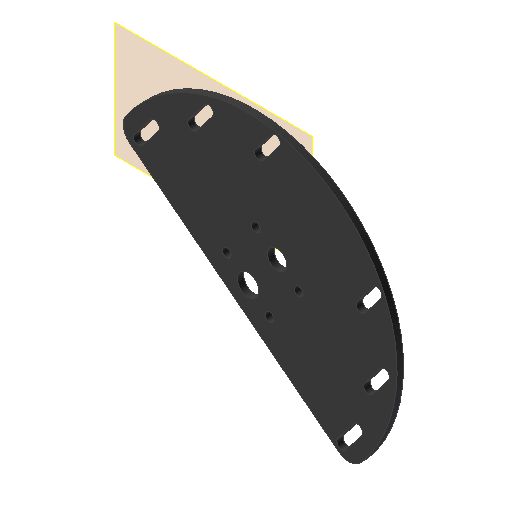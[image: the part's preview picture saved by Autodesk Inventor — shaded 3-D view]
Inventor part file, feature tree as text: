
AUTODESK INVENTOR PART (.ipt)
format: ipt  version: 2022 (Build 260153000, 153)  size: 200,704 bytes
history: native  units: mm
features: reference x10, other x5, extrude x2, sketch x2, plane x1, fillet x1, projected_geometry x1
ambient origin geometry x8: Origin, YZ Plane, XZ Plane, XY Plane, X Axis, Y Axis, Z Axis, Center Point
bodies: Volumenkörper1 (feature_tree)
feature tree (22):
  plane  "Arbeitsebene1"
  extrude  "Extrusion1"  Depth=2.0mm
  extrude  "Extrusion2"  Depth=5.0mm
  fillet  "Rundung1"  Radius=2.8mm
  sketch  "Skizze1"  dims[d0=2.0mm d1=0.0mm d2=2.8mm]
  reference  "Referenz1"
  reference  "Referenz2"
  reference  "Referenz3"
  reference  "Referenz4"
  reference  "Referenz5"
  reference  "Referenz6"
  reference  "Referenz7"
  reference  "Referenz8"
  reference  "Referenz9"
  reference  "Referenz10"
  sketch  "Skizze2"  dims[d3=2.8mm d4=2.8mm d5=2.8mm d6=4.0mm d7=3.1mm d8=3.1mm d9=3.1mm d10=3.1mm d11=3.1mm d12=3.1mm d13=3.1mm d14=2.0mm d15=0.0mm d16=5.0mm]
  projected_geometry  "Projizierte Kontur1"
  other  "Anglerfish_bonne_mamman_m12large_flipped_v0.iam"
  other  "Anglerfish_Lightplate_Tosslink_flipped:1"
  other  "Matchboxscope_M12_Lensadapter_v0:1"
  other  "00_toslink_launcher_v3:2"
  other  "00_toslink_launcher_v3:1"
